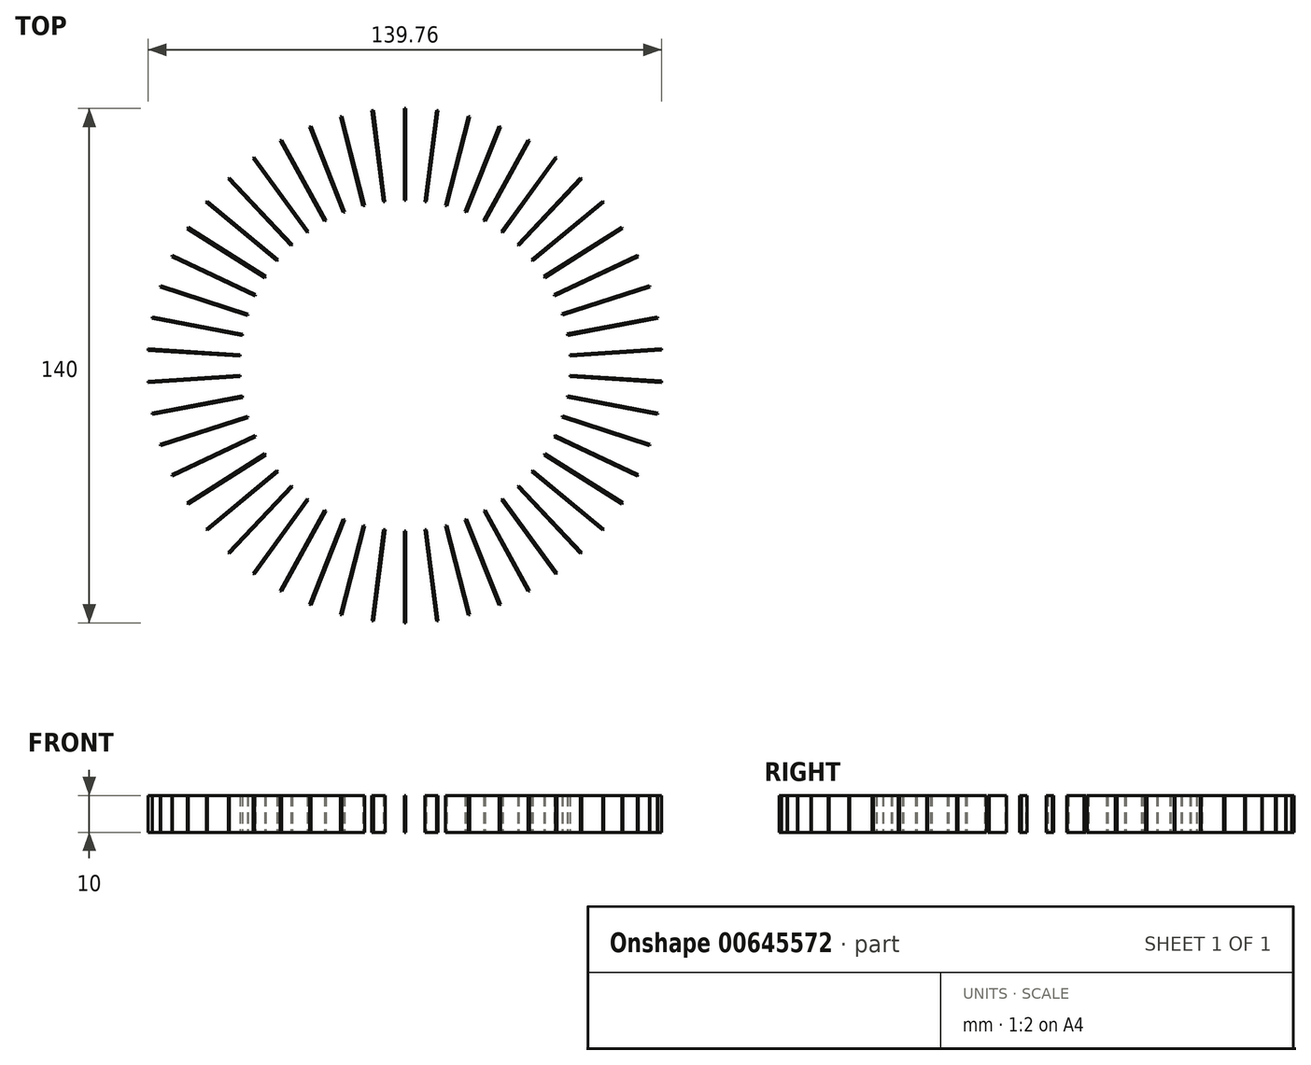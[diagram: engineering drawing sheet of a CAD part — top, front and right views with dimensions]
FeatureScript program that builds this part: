
annotation { "Feature Type Name" : "Feature", "Feature Type Description" : "" }
export const myFeature = defineFeature(function(context is Context, id is Id, definition is map)
    precondition{}
    {
        {
            var Q0;
            Q0=qCreatedBy(makeId("Top.planeOp"),FACE);
            var sketch = newSketch(context, id + "F0", { "sketchPlane" : qUnion([Q0])});
            skCircle(sketch, "E0", {"center": v(0, 0) * mm, "radius": 45 * mm, "construction": true});
            skCircle(sketch, "E1", {"center": v(0, 0) * mm, "radius": 70 * mm, "construction": true});
            skLineSegment(sketch, "E2.bottom", {"start": v(-0.22, 70) * mm, "end": v(0.2, 70) * mm});
            skLineSegment(sketch, "E2.top", {"start": v(-0.22, 45) * mm, "end": v(0.2, 45) * mm});
            skLineSegment(sketch, "E2.left", {"start": v(-0.22, 70) * mm, "end": v(-0.22, 45) * mm});
            skLineSegment(sketch, "E2.right", {"start": v(0.2, 70) * mm, "end": v(0.2, 45) * mm});
            skLineSegment(sketch, "E3.1.0", {"start": v(-8.99, 69.42) * mm, "end": v(-5.86, 44.62) * mm});
            skLineSegment(sketch, "E3.1.1", {"start": v(-8.58, 69.47) * mm, "end": v(-5.45, 44.67) * mm});
            skLineSegment(sketch, "E3.1.2", {"start": v(-5.86, 44.62) * mm, "end": v(-5.45, 44.67) * mm});
            skLineSegment(sketch, "E3.1.3", {"start": v(-8.99, 69.42) * mm, "end": v(-8.58, 69.47) * mm});
            skLineSegment(sketch, "E3.2.0", {"start": v(-17.62, 67.75) * mm, "end": v(-11.4, 43.53) * mm});
            skLineSegment(sketch, "E3.2.1", {"start": v(-17.22, 67.85) * mm, "end": v(-11, 43.63) * mm});
            skLineSegment(sketch, "E3.2.2", {"start": v(-11.4, 43.53) * mm, "end": v(-11, 43.63) * mm});
            skLineSegment(sketch, "E3.2.3", {"start": v(-17.62, 67.75) * mm, "end": v(-17.22, 67.85) * mm});
            skLineSegment(sketch, "E4.2.3.0", {"start": v(-25.97, 65) * mm, "end": v(-16.77, 41.76) * mm});
            skLineSegment(sketch, "E4.3.3.0", {"start": v(-25.59, 65.15) * mm, "end": v(-16.39, 41.91) * mm});
            skLineSegment(sketch, "E4.6.3.0", {"start": v(-16.77, 41.76) * mm, "end": v(-16.39, 41.91) * mm});
            skLineSegment(sketch, "E4.9.3.0", {"start": v(-25.97, 65) * mm, "end": v(-25.59, 65.15) * mm});
            skLineSegment(sketch, "E4.2.4.0", {"start": v(-33.91, 61.24) * mm, "end": v(-21.87, 39.33) * mm});
            skLineSegment(sketch, "E4.3.4.0", {"start": v(-33.55, 61.43) * mm, "end": v(-21.5, 39.53) * mm});
            skLineSegment(sketch, "E4.6.4.0", {"start": v(-21.87, 39.33) * mm, "end": v(-21.5, 39.53) * mm});
            skLineSegment(sketch, "E4.9.4.0", {"start": v(-33.91, 61.24) * mm, "end": v(-33.55, 61.43) * mm});
            skLineSegment(sketch, "E4.2.5.0", {"start": v(-41.32, 56.5) * mm, "end": v(-26.63, 36.28) * mm});
            skLineSegment(sketch, "E4.3.5.0", {"start": v(-40.99, 56.74) * mm, "end": v(-26.3, 36.52) * mm});
            skLineSegment(sketch, "E4.6.5.0", {"start": v(-26.63, 36.28) * mm, "end": v(-26.3, 36.52) * mm});
            skLineSegment(sketch, "E4.9.5.0", {"start": v(-41.32, 56.5) * mm, "end": v(-40.99, 56.74) * mm});
            skLineSegment(sketch, "E4.2.6.0", {"start": v(-48.08, 50.88) * mm, "end": v(-30.96, 32.65) * mm});
            skLineSegment(sketch, "E4.3.6.0", {"start": v(-47.78, 51.16) * mm, "end": v(-30.66, 32.94) * mm});
            skLineSegment(sketch, "E4.6.6.0", {"start": v(-30.96, 32.65) * mm, "end": v(-30.66, 32.94) * mm});
            skLineSegment(sketch, "E4.9.6.0", {"start": v(-48.08, 50.88) * mm, "end": v(-47.78, 51.16) * mm});
            skLineSegment(sketch, "E4.2.7.0", {"start": v(-54.07, 44.45) * mm, "end": v(-34.81, 28.52) * mm});
            skLineSegment(sketch, "E4.3.7.0", {"start": v(-53.81, 44.77) * mm, "end": v(-34.55, 28.83) * mm});
            skLineSegment(sketch, "E4.6.7.0", {"start": v(-34.81, 28.52) * mm, "end": v(-34.55, 28.83) * mm});
            skLineSegment(sketch, "E4.9.7.0", {"start": v(-54.07, 44.45) * mm, "end": v(-53.81, 44.77) * mm});
            skLineSegment(sketch, "E4.2.8.0", {"start": v(-59.22, 37.32) * mm, "end": v(-38.11, 23.93) * mm});
            skLineSegment(sketch, "E4.3.8.0", {"start": v(-59, 37.67) * mm, "end": v(-37.9, 24.27) * mm});
            skLineSegment(sketch, "E4.6.8.0", {"start": v(-38.11, 23.93) * mm, "end": v(-37.9, 24.27) * mm});
            skLineSegment(sketch, "E4.9.8.0", {"start": v(-59.22, 37.32) * mm, "end": v(-59, 37.67) * mm});
            skLineSegment(sketch, "E4.2.9.0", {"start": v(-63.43, 29.6) * mm, "end": v(-40.8, 18.96) * mm});
            skLineSegment(sketch, "E4.3.9.0", {"start": v(-63.26, 29.98) * mm, "end": v(-40.63, 19.33) * mm});
            skLineSegment(sketch, "E4.6.9.0", {"start": v(-40.8, 18.96) * mm, "end": v(-40.63, 19.33) * mm});
            skLineSegment(sketch, "E4.9.9.0", {"start": v(-63.43, 29.6) * mm, "end": v(-63.26, 29.98) * mm});
            skLineSegment(sketch, "E4.2.10.0", {"start": v(-66.64, 21.42) * mm, "end": v(-42.86, 13.7) * mm});
            skLineSegment(sketch, "E4.3.10.0", {"start": v(-66.51, 21.81) * mm, "end": v(-42.74, 14.09) * mm});
            skLineSegment(sketch, "E4.6.10.0", {"start": v(-42.86, 13.7) * mm, "end": v(-42.74, 14.09) * mm});
            skLineSegment(sketch, "E4.9.10.0", {"start": v(-66.64, 21.42) * mm, "end": v(-66.51, 21.81) * mm});
            skLineSegment(sketch, "E4.2.11.0", {"start": v(-68.8, 12.9) * mm, "end": v(-44.24, 8.22) * mm});
            skLineSegment(sketch, "E4.3.11.0", {"start": v(-68.72, 13.3) * mm, "end": v(-44.17, 8.62) * mm});
            skLineSegment(sketch, "E4.6.11.0", {"start": v(-44.24, 8.22) * mm, "end": v(-44.17, 8.62) * mm});
            skLineSegment(sketch, "E4.9.11.0", {"start": v(-68.8, 12.9) * mm, "end": v(-68.72, 13.3) * mm});
            skLineSegment(sketch, "E4.2.12.0", {"start": v(-69.88, 4.18) * mm, "end": v(-44.92, 2.6) * mm});
            skLineSegment(sketch, "E4.3.12.0", {"start": v(-69.85, 4.59) * mm, "end": v(-44.9, 3.02) * mm});
            skLineSegment(sketch, "E4.6.12.0", {"start": v(-44.92, 2.6) * mm, "end": v(-44.9, 3.02) * mm});
            skLineSegment(sketch, "E4.9.12.0", {"start": v(-69.88, 4.18) * mm, "end": v(-69.85, 4.59) * mm});
            skLineSegment(sketch, "E4.2.13.0", {"start": v(-69.85, -4.61) * mm, "end": v(-44.9, -3.04) * mm});
            skLineSegment(sketch, "E4.3.13.0", {"start": v(-69.87, -4.2) * mm, "end": v(-44.92, -2.63) * mm});
            skLineSegment(sketch, "E4.6.13.0", {"start": v(-44.9, -3.04) * mm, "end": v(-44.92, -2.63) * mm});
            skLineSegment(sketch, "E4.9.13.0", {"start": v(-69.85, -4.61) * mm, "end": v(-69.87, -4.2) * mm});
            skLineSegment(sketch, "E4.2.14.0", {"start": v(-68.72, -13.33) * mm, "end": v(-44.16, -8.65) * mm});
            skLineSegment(sketch, "E4.3.14.0", {"start": v(-68.8, -12.93) * mm, "end": v(-44.24, -8.24) * mm});
            skLineSegment(sketch, "E4.6.14.0", {"start": v(-44.16, -8.65) * mm, "end": v(-44.24, -8.24) * mm});
            skLineSegment(sketch, "E4.9.14.0", {"start": v(-68.72, -13.33) * mm, "end": v(-68.8, -12.93) * mm});
            skLineSegment(sketch, "E4.2.15.0", {"start": v(-66.5, -21.84) * mm, "end": v(-42.73, -14.11) * mm});
            skLineSegment(sketch, "E4.3.15.0", {"start": v(-66.63, -21.45) * mm, "end": v(-42.86, -13.72) * mm});
            skLineSegment(sketch, "E4.6.15.0", {"start": v(-42.73, -14.11) * mm, "end": v(-42.86, -13.72) * mm});
            skLineSegment(sketch, "E4.9.15.0", {"start": v(-66.5, -21.84) * mm, "end": v(-66.63, -21.45) * mm});
            skLineSegment(sketch, "E4.2.16.0", {"start": v(-63.25, -30) * mm, "end": v(-40.62, -19.36) * mm});
            skLineSegment(sketch, "E4.3.16.0", {"start": v(-63.42, -29.63) * mm, "end": v(-40.8, -18.99) * mm});
            skLineSegment(sketch, "E4.6.16.0", {"start": v(-40.62, -19.36) * mm, "end": v(-40.8, -18.99) * mm});
            skLineSegment(sketch, "E4.9.16.0", {"start": v(-63.25, -30) * mm, "end": v(-63.42, -29.63) * mm});
            skLineSegment(sketch, "E4.2.17.0", {"start": v(-58.99, -37.7) * mm, "end": v(-37.88, -24.3) * mm});
            skLineSegment(sketch, "E4.3.17.0", {"start": v(-59.2, -37.34) * mm, "end": v(-38.1, -23.95) * mm});
            skLineSegment(sketch, "E4.6.17.0", {"start": v(-37.88, -24.3) * mm, "end": v(-38.1, -23.95) * mm});
            skLineSegment(sketch, "E4.9.17.0", {"start": v(-58.99, -37.7) * mm, "end": v(-59.2, -37.34) * mm});
            skLineSegment(sketch, "E4.2.18.0", {"start": v(-53.8, -44.79) * mm, "end": v(-34.53, -28.85) * mm});
            skLineSegment(sketch, "E4.3.18.0", {"start": v(-54.06, -44.47) * mm, "end": v(-34.8, -28.54) * mm});
            skLineSegment(sketch, "E4.6.18.0", {"start": v(-34.53, -28.85) * mm, "end": v(-34.8, -28.54) * mm});
            skLineSegment(sketch, "E4.9.18.0", {"start": v(-53.8, -44.79) * mm, "end": v(-54.06, -44.47) * mm});
            skLineSegment(sketch, "E4.2.19.0", {"start": v(-47.76, -51.18) * mm, "end": v(-30.65, -32.95) * mm});
            skLineSegment(sketch, "E4.3.19.0", {"start": v(-48.06, -50.9) * mm, "end": v(-30.94, -32.67) * mm});
            skLineSegment(sketch, "E4.6.19.0", {"start": v(-30.65, -32.95) * mm, "end": v(-30.94, -32.67) * mm});
            skLineSegment(sketch, "E4.9.19.0", {"start": v(-47.76, -51.18) * mm, "end": v(-48.06, -50.9) * mm});
            skLineSegment(sketch, "E4.2.20.0", {"start": v(-40.97, -56.76) * mm, "end": v(-26.27, -36.53) * mm});
            skLineSegment(sketch, "E4.3.20.0", {"start": v(-41.3, -56.52) * mm, "end": v(-26.6, -36.3) * mm});
            skLineSegment(sketch, "E4.6.20.0", {"start": v(-26.27, -36.53) * mm, "end": v(-26.6, -36.3) * mm});
            skLineSegment(sketch, "E4.9.20.0", {"start": v(-40.97, -56.76) * mm, "end": v(-41.3, -56.52) * mm});
            skLineSegment(sketch, "E4.2.21.0", {"start": v(-33.53, -61.45) * mm, "end": v(-21.49, -39.54) * mm});
            skLineSegment(sketch, "E4.3.21.0", {"start": v(-33.9, -61.25) * mm, "end": v(-21.85, -39.34) * mm});
            skLineSegment(sketch, "E4.6.21.0", {"start": v(-21.49, -39.54) * mm, "end": v(-21.85, -39.34) * mm});
            skLineSegment(sketch, "E4.9.21.0", {"start": v(-33.53, -61.45) * mm, "end": v(-33.9, -61.25) * mm});
            skLineSegment(sketch, "E4.2.22.0", {"start": v(-25.57, -65.16) * mm, "end": v(-16.36, -41.92) * mm});
            skLineSegment(sketch, "E4.3.22.0", {"start": v(-25.95, -65.01) * mm, "end": v(-16.74, -41.77) * mm});
            skLineSegment(sketch, "E4.6.22.0", {"start": v(-16.36, -41.92) * mm, "end": v(-16.74, -41.77) * mm});
            skLineSegment(sketch, "E4.9.22.0", {"start": v(-25.57, -65.16) * mm, "end": v(-25.95, -65.01) * mm});
            skLineSegment(sketch, "E4.2.23.0", {"start": v(-17.2, -67.85) * mm, "end": v(-10.98, -43.64) * mm});
            skLineSegment(sketch, "E4.3.23.0", {"start": v(-17.6, -67.75) * mm, "end": v(-11.38, -43.54) * mm});
            skLineSegment(sketch, "E4.6.23.0", {"start": v(-10.98, -43.64) * mm, "end": v(-11.38, -43.54) * mm});
            skLineSegment(sketch, "E4.9.23.0", {"start": v(-17.2, -67.85) * mm, "end": v(-17.6, -67.75) * mm});
            skLineSegment(sketch, "E4.2.24.0", {"start": v(-8.56, -69.47) * mm, "end": v(-5.42, -44.67) * mm});
            skLineSegment(sketch, "E4.3.24.0", {"start": v(-8.96, -69.42) * mm, "end": v(-5.83, -44.62) * mm});
            skLineSegment(sketch, "E4.6.24.0", {"start": v(-5.42, -44.67) * mm, "end": v(-5.83, -44.62) * mm});
            skLineSegment(sketch, "E4.9.24.0", {"start": v(-8.56, -69.47) * mm, "end": v(-8.96, -69.42) * mm});
            skLineSegment(sketch, "E4.2.25.0", {"start": v(0.22, -70) * mm, "end": v(0.22, -45) * mm});
            skLineSegment(sketch, "E4.3.25.0", {"start": v(-0.2, -70) * mm, "end": v(-0.2, -45) * mm});
            skLineSegment(sketch, "E4.6.25.0", {"start": v(0.22, -45) * mm, "end": v(-0.2, -45) * mm});
            skLineSegment(sketch, "E4.9.25.0", {"start": v(0.22, -70) * mm, "end": v(-0.2, -70) * mm});
            skLineSegment(sketch, "E4.2.26.0", {"start": v(8.99, -69.42) * mm, "end": v(5.86, -44.62) * mm});
            skLineSegment(sketch, "E4.3.26.0", {"start": v(8.58, -69.47) * mm, "end": v(5.45, -44.67) * mm});
            skLineSegment(sketch, "E4.6.26.0", {"start": v(5.86, -44.62) * mm, "end": v(5.45, -44.67) * mm});
            skLineSegment(sketch, "E4.9.26.0", {"start": v(8.99, -69.42) * mm, "end": v(8.58, -69.47) * mm});
            skLineSegment(sketch, "E4.2.27.0", {"start": v(17.62, -67.75) * mm, "end": v(11.4, -43.53) * mm});
            skLineSegment(sketch, "E4.3.27.0", {"start": v(17.22, -67.85) * mm, "end": v(11, -43.63) * mm});
            skLineSegment(sketch, "E4.6.27.0", {"start": v(11.4, -43.53) * mm, "end": v(11, -43.63) * mm});
            skLineSegment(sketch, "E4.9.27.0", {"start": v(17.62, -67.75) * mm, "end": v(17.22, -67.85) * mm});
            skLineSegment(sketch, "E4.2.28.0", {"start": v(25.97, -65) * mm, "end": v(16.77, -41.76) * mm});
            skLineSegment(sketch, "E4.3.28.0", {"start": v(25.59, -65.15) * mm, "end": v(16.39, -41.91) * mm});
            skLineSegment(sketch, "E4.6.28.0", {"start": v(16.77, -41.76) * mm, "end": v(16.39, -41.91) * mm});
            skLineSegment(sketch, "E4.9.28.0", {"start": v(25.97, -65) * mm, "end": v(25.59, -65.15) * mm});
            skLineSegment(sketch, "E4.2.29.0", {"start": v(33.91, -61.24) * mm, "end": v(21.87, -39.33) * mm});
            skLineSegment(sketch, "E4.3.29.0", {"start": v(33.55, -61.43) * mm, "end": v(21.5, -39.53) * mm});
            skLineSegment(sketch, "E4.6.29.0", {"start": v(21.87, -39.33) * mm, "end": v(21.5, -39.53) * mm});
            skLineSegment(sketch, "E4.9.29.0", {"start": v(33.91, -61.24) * mm, "end": v(33.55, -61.43) * mm});
            skLineSegment(sketch, "E4.2.30.0", {"start": v(41.32, -56.5) * mm, "end": v(26.63, -36.28) * mm});
            skLineSegment(sketch, "E4.3.30.0", {"start": v(40.99, -56.74) * mm, "end": v(26.3, -36.52) * mm});
            skLineSegment(sketch, "E4.6.30.0", {"start": v(26.63, -36.28) * mm, "end": v(26.3, -36.52) * mm});
            skLineSegment(sketch, "E4.9.30.0", {"start": v(41.32, -56.5) * mm, "end": v(40.99, -56.74) * mm});
            skLineSegment(sketch, "E4.2.31.0", {"start": v(48.08, -50.88) * mm, "end": v(30.96, -32.65) * mm});
            skLineSegment(sketch, "E4.3.31.0", {"start": v(47.78, -51.16) * mm, "end": v(30.66, -32.94) * mm});
            skLineSegment(sketch, "E4.6.31.0", {"start": v(30.96, -32.65) * mm, "end": v(30.66, -32.94) * mm});
            skLineSegment(sketch, "E4.9.31.0", {"start": v(48.08, -50.88) * mm, "end": v(47.78, -51.16) * mm});
            skLineSegment(sketch, "E4.2.32.0", {"start": v(54.07, -44.45) * mm, "end": v(34.81, -28.52) * mm});
            skLineSegment(sketch, "E4.3.32.0", {"start": v(53.81, -44.77) * mm, "end": v(34.55, -28.83) * mm});
            skLineSegment(sketch, "E4.6.32.0", {"start": v(34.81, -28.52) * mm, "end": v(34.55, -28.83) * mm});
            skLineSegment(sketch, "E4.9.32.0", {"start": v(54.07, -44.45) * mm, "end": v(53.81, -44.77) * mm});
            skLineSegment(sketch, "E4.2.33.0", {"start": v(59.22, -37.32) * mm, "end": v(38.11, -23.93) * mm});
            skLineSegment(sketch, "E4.3.33.0", {"start": v(59, -37.67) * mm, "end": v(37.9, -24.27) * mm});
            skLineSegment(sketch, "E4.6.33.0", {"start": v(38.11, -23.93) * mm, "end": v(37.9, -24.27) * mm});
            skLineSegment(sketch, "E4.9.33.0", {"start": v(59.22, -37.32) * mm, "end": v(59, -37.67) * mm});
            skLineSegment(sketch, "E4.2.34.0", {"start": v(63.43, -29.6) * mm, "end": v(40.8, -18.96) * mm});
            skLineSegment(sketch, "E4.3.34.0", {"start": v(63.26, -29.98) * mm, "end": v(40.63, -19.33) * mm});
            skLineSegment(sketch, "E4.6.34.0", {"start": v(40.8, -18.96) * mm, "end": v(40.63, -19.33) * mm});
            skLineSegment(sketch, "E4.9.34.0", {"start": v(63.43, -29.6) * mm, "end": v(63.26, -29.98) * mm});
            skLineSegment(sketch, "E4.2.35.0", {"start": v(66.64, -21.42) * mm, "end": v(42.86, -13.7) * mm});
            skLineSegment(sketch, "E4.3.35.0", {"start": v(66.51, -21.81) * mm, "end": v(42.74, -14.09) * mm});
            skLineSegment(sketch, "E4.6.35.0", {"start": v(42.86, -13.7) * mm, "end": v(42.74, -14.09) * mm});
            skLineSegment(sketch, "E4.9.35.0", {"start": v(66.64, -21.42) * mm, "end": v(66.51, -21.81) * mm});
            skLineSegment(sketch, "E4.2.36.0", {"start": v(68.8, -12.9) * mm, "end": v(44.24, -8.22) * mm});
            skLineSegment(sketch, "E4.3.36.0", {"start": v(68.72, -13.3) * mm, "end": v(44.17, -8.62) * mm});
            skLineSegment(sketch, "E4.6.36.0", {"start": v(44.24, -8.22) * mm, "end": v(44.17, -8.62) * mm});
            skLineSegment(sketch, "E4.9.36.0", {"start": v(68.8, -12.9) * mm, "end": v(68.72, -13.3) * mm});
            skLineSegment(sketch, "E4.2.37.0", {"start": v(69.88, -4.18) * mm, "end": v(44.92, -2.6) * mm});
            skLineSegment(sketch, "E4.3.37.0", {"start": v(69.85, -4.59) * mm, "end": v(44.9, -3.02) * mm});
            skLineSegment(sketch, "E4.6.37.0", {"start": v(44.92, -2.6) * mm, "end": v(44.9, -3.02) * mm});
            skLineSegment(sketch, "E4.9.37.0", {"start": v(69.88, -4.18) * mm, "end": v(69.85, -4.59) * mm});
            skLineSegment(sketch, "E4.2.38.0", {"start": v(69.85, 4.61) * mm, "end": v(44.9, 3.04) * mm});
            skLineSegment(sketch, "E4.3.38.0", {"start": v(69.87, 4.2) * mm, "end": v(44.92, 2.63) * mm});
            skLineSegment(sketch, "E4.6.38.0", {"start": v(44.9, 3.04) * mm, "end": v(44.92, 2.63) * mm});
            skLineSegment(sketch, "E4.9.38.0", {"start": v(69.85, 4.61) * mm, "end": v(69.87, 4.2) * mm});
            skLineSegment(sketch, "E4.2.39.0", {"start": v(68.72, 13.33) * mm, "end": v(44.16, 8.65) * mm});
            skLineSegment(sketch, "E4.3.39.0", {"start": v(68.8, 12.93) * mm, "end": v(44.24, 8.24) * mm});
            skLineSegment(sketch, "E4.6.39.0", {"start": v(44.16, 8.65) * mm, "end": v(44.24, 8.24) * mm});
            skLineSegment(sketch, "E4.9.39.0", {"start": v(68.72, 13.33) * mm, "end": v(68.8, 12.93) * mm});
            skLineSegment(sketch, "E4.2.40.0", {"start": v(66.5, 21.84) * mm, "end": v(42.73, 14.11) * mm});
            skLineSegment(sketch, "E4.3.40.0", {"start": v(66.63, 21.45) * mm, "end": v(42.86, 13.72) * mm});
            skLineSegment(sketch, "E4.6.40.0", {"start": v(42.73, 14.11) * mm, "end": v(42.86, 13.72) * mm});
            skLineSegment(sketch, "E4.9.40.0", {"start": v(66.5, 21.84) * mm, "end": v(66.63, 21.45) * mm});
            skLineSegment(sketch, "E4.2.41.0", {"start": v(63.25, 30) * mm, "end": v(40.62, 19.36) * mm});
            skLineSegment(sketch, "E4.3.41.0", {"start": v(63.42, 29.63) * mm, "end": v(40.8, 18.99) * mm});
            skLineSegment(sketch, "E4.6.41.0", {"start": v(40.62, 19.36) * mm, "end": v(40.8, 18.99) * mm});
            skLineSegment(sketch, "E4.9.41.0", {"start": v(63.25, 30) * mm, "end": v(63.42, 29.63) * mm});
            skLineSegment(sketch, "E4.2.42.0", {"start": v(58.99, 37.7) * mm, "end": v(37.88, 24.3) * mm});
            skLineSegment(sketch, "E4.3.42.0", {"start": v(59.2, 37.34) * mm, "end": v(38.1, 23.95) * mm});
            skLineSegment(sketch, "E4.6.42.0", {"start": v(37.88, 24.3) * mm, "end": v(38.1, 23.95) * mm});
            skLineSegment(sketch, "E4.9.42.0", {"start": v(58.99, 37.7) * mm, "end": v(59.2, 37.34) * mm});
            skLineSegment(sketch, "E4.2.43.0", {"start": v(53.8, 44.79) * mm, "end": v(34.53, 28.85) * mm});
            skLineSegment(sketch, "E4.3.43.0", {"start": v(54.06, 44.47) * mm, "end": v(34.8, 28.54) * mm});
            skLineSegment(sketch, "E4.6.43.0", {"start": v(34.53, 28.85) * mm, "end": v(34.8, 28.54) * mm});
            skLineSegment(sketch, "E4.9.43.0", {"start": v(53.8, 44.79) * mm, "end": v(54.06, 44.47) * mm});
            skLineSegment(sketch, "E4.2.44.0", {"start": v(47.76, 51.18) * mm, "end": v(30.65, 32.95) * mm});
            skLineSegment(sketch, "E4.3.44.0", {"start": v(48.06, 50.9) * mm, "end": v(30.94, 32.67) * mm});
            skLineSegment(sketch, "E4.6.44.0", {"start": v(30.65, 32.95) * mm, "end": v(30.94, 32.67) * mm});
            skLineSegment(sketch, "E4.9.44.0", {"start": v(47.76, 51.18) * mm, "end": v(48.06, 50.9) * mm});
            skLineSegment(sketch, "E5.2.45.0", {"start": v(40.97, 56.76) * mm, "end": v(26.27, 36.53) * mm});
            skLineSegment(sketch, "E5.3.45.0", {"start": v(41.3, 56.52) * mm, "end": v(26.6, 36.3) * mm});
            skLineSegment(sketch, "E5.6.45.0", {"start": v(26.27, 36.53) * mm, "end": v(26.6, 36.3) * mm});
            skLineSegment(sketch, "E5.9.45.0", {"start": v(40.97, 56.76) * mm, "end": v(41.3, 56.52) * mm});
            skLineSegment(sketch, "E5.2.46.0", {"start": v(33.53, 61.45) * mm, "end": v(21.49, 39.54) * mm});
            skLineSegment(sketch, "E5.3.46.0", {"start": v(33.9, 61.25) * mm, "end": v(21.85, 39.34) * mm});
            skLineSegment(sketch, "E5.6.46.0", {"start": v(21.49, 39.54) * mm, "end": v(21.85, 39.34) * mm});
            skLineSegment(sketch, "E5.9.46.0", {"start": v(33.53, 61.45) * mm, "end": v(33.9, 61.25) * mm});
            skLineSegment(sketch, "E5.2.47.0", {"start": v(25.57, 65.16) * mm, "end": v(16.36, 41.92) * mm});
            skLineSegment(sketch, "E5.3.47.0", {"start": v(25.95, 65.01) * mm, "end": v(16.74, 41.77) * mm});
            skLineSegment(sketch, "E5.6.47.0", {"start": v(16.36, 41.92) * mm, "end": v(16.74, 41.77) * mm});
            skLineSegment(sketch, "E5.9.47.0", {"start": v(25.57, 65.16) * mm, "end": v(25.95, 65.01) * mm});
            skLineSegment(sketch, "E5.2.48.0", {"start": v(17.2, 67.85) * mm, "end": v(10.98, 43.64) * mm});
            skLineSegment(sketch, "E5.3.48.0", {"start": v(17.6, 67.75) * mm, "end": v(11.38, 43.54) * mm});
            skLineSegment(sketch, "E5.6.48.0", {"start": v(10.98, 43.64) * mm, "end": v(11.38, 43.54) * mm});
            skLineSegment(sketch, "E5.9.48.0", {"start": v(17.2, 67.85) * mm, "end": v(17.6, 67.75) * mm});
            skLineSegment(sketch, "E5.2.49.0", {"start": v(8.56, 69.47) * mm, "end": v(5.42, 44.67) * mm});
            skLineSegment(sketch, "E5.3.49.0", {"start": v(8.96, 69.42) * mm, "end": v(5.83, 44.62) * mm});
            skLineSegment(sketch, "E5.6.49.0", {"start": v(5.42, 44.67) * mm, "end": v(5.83, 44.62) * mm});
            skLineSegment(sketch, "E5.9.49.0", {"start": v(8.56, 69.47) * mm, "end": v(8.96, 69.42) * mm});
            skSolve(sketch);
        }
        {
            var Q0;
            Q0 = qSketchRegion(id + "F0", true);
            extrude(context, id + "F1", {"entities" : qUnion([Q0]), "depth" : 10 * mm, "offsetDistance" : 25 * mm});
        }
    });
